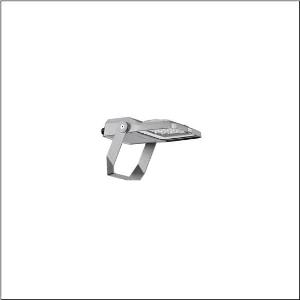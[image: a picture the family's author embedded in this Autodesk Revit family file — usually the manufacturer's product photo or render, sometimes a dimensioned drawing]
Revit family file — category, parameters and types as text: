
# Revit family: floodlight_fl_21_iq_micro___rs12_5xa7762a1b1a_c11c
name_source: partatom
category: Lighting Fixtures
units: mm (PartAtom-declared; Revit-internal decimal feet)

## family parameters
Cut with Voids When Loaded = No
Host = Face
Light Source = No
Part Type = Normal
Room Calculation Point = No
Round Connector Dimension = Use Diameter
Shared = No

## types (1)
- --- (1 x LED, 2560 lm, 23.1 W, 2200K)
    Apparent Load = 23 VA
    CIE Flux Codes = 79 92 99 100 100
    Color Rendering = 70
    Color Temperature = 2200K
    Default Elevation = 1800 mm
    Description = Floodlight FL 21 iQ micro, floodlight, primary light control with lens, of PMMA, primary optical cover: protective disc, of toughened safety glass, transparent, light distribution: RS12, light emission: direct distribution, installation type: surface-mounted, LED, High Power LED, rated luminous flux: 2.560lm, luminous efficacy: 111lm/W, light colour: 722, colour temperature: 2200K, control: Auto-Match, Temp-Guard, Night-Set, Smart-Wire, Desk-Remote (wireless, voltage-free reading and setting of iQ features in the workshop via application-optimized NFC function/RFID function), optimised constant luminous flux control (CLO 2.0), Street-Remote, with terminal, 6-pole, mains connection: 220..240V, AC, 50/60Hz, start of lifetime: 23W, end of service life: 24W, reduction: 11W, luminaire housing, of diecast aluminium, powder-coated, Siteco® metallic grey (DB 702S), corrosivity category C5 mid according to DIN EN ISO 12944, sealing non-destructively replaceable, mounting bracket, of steel, galvanised, powder-coated, Siteco® metallic grey (DB 702S), protection rating (complete): IP66, insulation class (complete): insulation class II (safety insulation), certification: CE, ENEC, VDE, protection symbol: D, impact resistance: IK07, permissible operating ambient temperature: -40..+40°C, permissible operating ambient temperature for outdoor applications: -40..+50°C, standard: DIN EN 12944, LABS conformity tested according to VDMA 24364:2018-05, packaging unit: 1 piece

Light Distribution: RS12
    Height = 65 mm
    Lamp = 1 x LED
    Lamp Light Flux = 2560 lm
    Lamp Power = 23.1 W
    Lamp count = 1
    Length = 312 mm
    Luminous efficacy = 111 lm/W
    Manufacturer = Siteco
    ModVariant = No
    Model = 5XA7762A1B1A
    Number of Poles = 1
    OnlyDefault = Yes
    Power Factor = 1
    Product Name = Floodlight FL 21 iQ micro | RS12
    Product group = floodlight | pylon annexe
    ProductGroupID = 6200
    Protection Class = Protection class II
    Protection Degree = IP 66
    RLX_Detail_Level = 1
    RLX_Emergency_Light_Flux = 0 lm
    RLX_Emergency_Type = 0
    RLX_Emergency_Type_DB = No
    RlxData = <blob elided: 75225 chars, md5=cf66110c>
    Socket = socket
    Standby Power = 0 W
    System Light Flux = 2560 lm
    System Power = 23 W
    Type Comments = factory setting: luminous flux: 100 % | dim-lin: 254 | 455 mA
    Type Image = l_1006880.jpg
    URL = http://relux.com
    VarID = @adj_153403
    Voltage = 0 V
    Weight = 0.00 kg
    Width = 230 mm

## geometry (parser evidence)
native form markers: Blend x4, Sweep x10
no freeform markers — native parametric forms only
